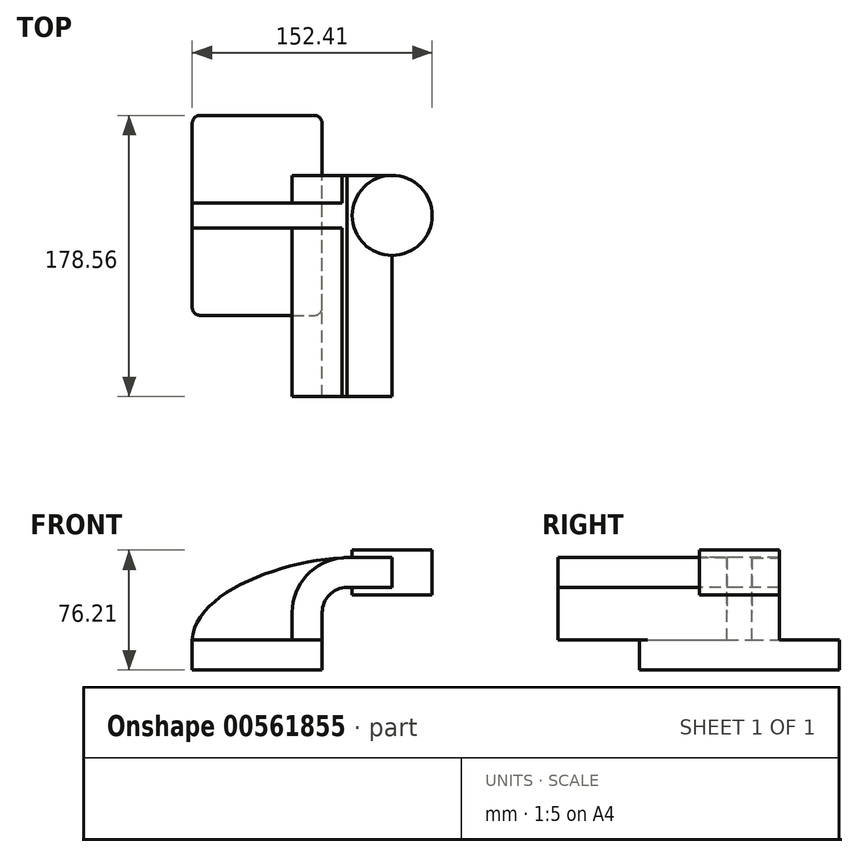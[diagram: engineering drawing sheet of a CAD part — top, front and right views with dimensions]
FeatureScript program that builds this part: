
annotation { "Feature Type Name" : "Feature", "Feature Type Description" : "" }
export const myFeature = defineFeature(function(context is Context, id is Id, definition is map)
    precondition{}
    {
        {
            var Q0;
            Q0=qCreatedBy(makeId("Front.planeOp"),FACE);
            var sketch = newSketch(context, id + "F0", { "sketchPlane" : qUnion([Q0])});
            skLineSegment(sketch, "E0.rect.bottom", {"start": v(-41.28, 9.52) * mm, "end": v(41.28, 9.52) * mm});
            skLineSegment(sketch, "E0.rect.top", {"start": v(-41.28, -9.52) * mm, "end": v(41.28, -9.52) * mm});
            skLineSegment(sketch, "E0.rect.left", {"start": v(-41.28, 9.52) * mm, "end": v(-41.28, -9.52) * mm});
            skLineSegment(sketch, "E0.rect.right", {"start": v(41.28, 9.52) * mm, "end": v(41.28, -9.52) * mm});
            skPoint(sketch, "E0.rect.middle", {"position": v(0, 0) * mm});
            skLineSegment(sketch, "E1", {"start": v(41.28, 9.52) * mm, "end": v(41.28, 27) * mm});
            skArc(sketch, "E2", {"start": v(41.28, 27) * mm, "mid": v(45.92, 38.23) * mm, "end": v(57.15, 42.88) * mm});
            skLineSegment(sketch, "E3", {"start": v(57.15, 42.88) * mm, "end": v(85.72, 42.88) * mm});
            skLineSegment(sketch, "E4.rect.bottom", {"start": v(60.32, 38.1) * mm, "end": v(111.12, 38.1) * mm});
            skLineSegment(sketch, "E4.rect.top", {"start": v(60.32, 66.68) * mm, "end": v(111.12, 66.68) * mm});
            skLineSegment(sketch, "E4.rect.left", {"start": v(60.32, 38.1) * mm, "end": v(60.32, 66.68) * mm});
            skLineSegment(sketch, "E4.rect.right", {"start": v(111.13, 38.1) * mm, "end": v(111.12, 66.68) * mm});
            skPoint(sketch, "E4.rect.middle", {"position": v(85.72, 52.39) * mm});
            skLineSegment(sketch, "E5.0", {"start": v(57.15, 61.93) * mm, "end": v(85.72, 61.93) * mm});
            skArc(sketch, "E5.1", {"start": v(22.23, 27) * mm, "mid": v(32.45, 51.7) * mm, "end": v(57.15, 61.93) * mm});
            skLineSegment(sketch, "E5.2", {"start": v(22.23, 9.52) * mm, "end": v(22.23, 27) * mm});
            skLineSegment(sketch, "E6", {"start": v(85.72, 38.1) * mm, "end": v(85.72, 66.68) * mm});
            skFitSpline(sketch, "E7", {"points": [v(-41.28, 9.53) * mm, v(57.15, 61.93) * mm], "startDerivative": vector(5.2, 92.34) * mm, "endDerivative": vector(120.92, 4.22) * mm});
            skSolve(sketch);
        }
        {
            var Q0;
            Q0=makeQuery(id+"F0.imprint","IMPRINT",FACE,{"disambiguationData":[TD([[makeQuery(id+"F0.imprint","IMPRINT",EDGE,{"derivedFrom":sQuery(id+"F0.wireOp",EDGE,"E0.rect.top")}),1.0]])]});
            extrude(context, id + "F1", {"entities" : qUnion([Q0]), "endBound" : BoundingType.SYMMETRIC, "depth" : 127 * mm});
        }
        {
            var Q0;
            {var subQ9=sQuery(id+"F0.wireOp",EDGE,"E1");Q0=makeQuery(id+"F0.imprint","IMPRINT",FACE,{"disambiguationData":[TD([[makeQuery(id+"F0.imprint","IMPRINT",EDGE,{"derivedFrom":subQ9}),1.0]])]});}
            var Q1;
            {var subQ0=sQuery(id+"F0.wireOp",EDGE,"E6");var subQ1=sQuery(id+"F0.wireOp",EDGE,"E3");var subQ2=makeQuery(id+"F0.imprint","INTERSECT",VERTEX,{"derivedFrom":[subQ1,subQ0]});Q1=makeQuery(id+"F0.imprint","IMPRINT",FACE,{"disambiguationData":[TD([[makeQuery(id+"F0.imprint","IMPRINT",EDGE,{"disambiguationData":[TD([[subQ2,1.0]])],"derivedFrom":subQ1}),1.0]])]});}
            extrude(context, id + "F2", {"entities" : qUnion([Q0, Q1]), "operationType" : NewBodyOperationType.ADD, "endBound" : BoundingType.SYMMETRIC, "depth" : 50.8 * mm});
        }
        {
            var Q0;
            {var subQ3=sQuery(id+"F0.wireOp",EDGE,"E5.2");Q0=makeQuery(id+"F0.imprint","IMPRINT",FACE,{"disambiguationData":[TD([[makeQuery(id+"F0.imprint","IMPRINT",EDGE,{"derivedFrom":subQ3}),1.0]])]});}
            extrude(context, id + "F3", {"entities" : qUnion([Q0]), "operationType" : NewBodyOperationType.ADD, "endBound" : BoundingType.SYMMETRIC, "depth" : 15.88 * mm});
        }
        {
            var Q0;
            {var subQ5=sQuery(id+"F0.wireOp",EDGE,"E4.rect.right");Q0=makeQuery(id+"F0.imprint","IMPRINT",FACE,{"disambiguationData":[TD([[makeQuery(id+"F0.imprint","IMPRINT",EDGE,{"derivedFrom":subQ5}),1.0]])]});}
            var Q1;
            Q1=sQuery(id+"F0.wireOp",EDGE,"E6");
            revolve(context, id + "F4", {"operationType" : NewBodyOperationType.ADD, "entities" : qUnion([Q0]), "axis" : qUnion([Q1]), "revolveType" : RevolveType.FULL});
        }
        {
            var Q0;
            Q0=makeQuery(id+"F1.opExtrude","CAP_EDGE",EDGE,{"disambiguationData":[OSD([sQuery(id+"F0.wireOp",EDGE,"E0.rect.right")])],"isStart":false});
            var Q1;
            Q1=makeQuery(id+"F1.opExtrude","CAP_EDGE",EDGE,{"disambiguationData":[OSD([sQuery(id+"F0.wireOp",EDGE,"E0.rect.left")])],"isStart":false});
            var Q2;
            Q2=makeQuery(id+"F1.opExtrude","CAP_EDGE",EDGE,{"disambiguationData":[OSD([sQuery(id+"F0.wireOp",EDGE,"E0.rect.right")])],"isStart":true});
            var Q3;
            Q3=makeQuery(id+"F1.opExtrude","CAP_EDGE",EDGE,{"disambiguationData":[OSD([sQuery(id+"F0.wireOp",EDGE,"E0.rect.left")])],"isStart":true});
            fillet(context, id + "F5", {"entities" : qUnion([Q0, Q1, Q2, Q3]), "radius" : 5.08 * mm, "tangentPropagation" : true, "allowEdgeOverflow" : false});
        }
        {
            var Q0;
            Q0=makeQuery(id+"F2.opExtrude","CAP_FACE",FACE,{"disambiguationData":[OSD([sQuery(id+"F0.wireOp",EDGE,"E0.rect.bottom"),sQuery(id+"F0.wireOp",EDGE,"E1"),sQuery(id+"F0.wireOp",EDGE,"E2"),sQuery(id+"F0.wireOp",EDGE,"E3"),sQuery(id+"F0.wireOp",EDGE,"E5.0"),sQuery(id+"F0.wireOp",EDGE,"E5.1"),sQuery(id+"F0.wireOp",EDGE,"E5.2"),sQuery(id+"F0.wireOp",EDGE,"E6"),sQuery(id+"F0.wireOp",EDGE,"E7")])],"isStart":false});
            extrude(context, id + "F6", {"entities" : qUnion([Q0]), "operationType" : NewBodyOperationType.ADD, "depth" : 89.66 * mm, "offsetDistance" : 25.4 * mm});
        }
    });
